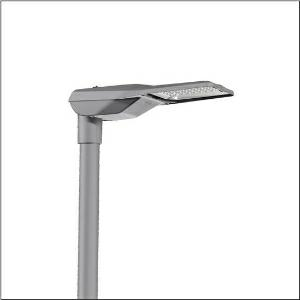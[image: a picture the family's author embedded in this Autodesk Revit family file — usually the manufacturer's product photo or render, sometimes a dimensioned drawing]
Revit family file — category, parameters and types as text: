
# Revit family: streetlight_sl_21_mini___p0_8ab_5xe2r33s08jb_3409
name_source: partatom
category: Lighting Fixtures
units: mm (PartAtom-declared; Revit-internal decimal feet)

## family parameters
Cut with Voids When Loaded = No
Host = Face
Light Source = No
Part Type = Normal
Room Calculation Point = No
Round Connector Dimension = Use Diameter
Shared = No

## types (1)
- --- (1 x LED, 11230 lm, 88.6 W, 3000K)
    Apparent Load = 89 VA
    CIE Flux Codes = 39 72 97 100 100
    Color Rendering = 70
    Color Temperature = 3000K
    Default Elevation = 1800 mm
    Description = Streetlight SL 21 mini, mast luminaire, primary light control with lens, of PMMA, primary optical cover: cover, of toughened safety glass, transparent, light distribution: P0.8aB, light emission: direct distribution, primary light characteristic: asymmetric, installation type: post-top, side-entry, LED, High Power LED, rated luminous flux: 11.230lm, luminous efficacy: 127lm/W, light colour: 730, colour temperature: 3000K, control gear: D4i, control: pre-setting: logarithmic dimming characteristic, flexible luminous flux parameterisation, time-dependent luminous flux control, constant luminous flux control, overheat protection, mains connection: 220..240V, AC, 50/60Hz, start of lifetime: 89W, end of service life: 92W, reduction: 41W, luminaire housing, of diecast aluminium, powder-coated, Siteco® metallic grey (DB 702S), corrosivity category C5 mid according to DIN EN ISO 12944, multi-level sealing system, sealing non-destructively replaceable, inclination adjustable: 0°, 5°, 10°, 15°, please order mast flange separately, length: 628mm, width: 235mm, height: 110mm, mast flange for spigot size: 42mm (side-entry): 5XC10008XM4, 60/48mm (side-entry/post-top): 5XC10108XM2, 76/60mm (side-entry/post-top): 5XC10108XM1, mounting height: 4..8m, Smart Interface above, protection rating (complete): IP66, insulation class (complete): insulation class II (safety insulation), certification: CE, ENEC, ENEC+, VDE, impact resistance: IK10, permissible operating ambient temperature for outdoor applications: -40..+50°C, standard-compliant lighting for roads and squares, packaging unit: 1 piece

Light Distribution: P0.8aB
    Height = 110 mm
    Lamp = 1 x LED
    Lamp Light Flux = 11230 lm
    Lamp Power = 88.6 W
    Lamp count = 1
    Length = 625 mm
    Luminous efficacy = 127 lm/W
    Manufacturer = Siteco
    ModVariant = No
    Model = 5XE2R33S08JB
    Number of Poles = 1
    OnlyDefault = Yes
    Power Factor = 1
    Product Name = Streetlight SL 21 mini | P0.8aB
    Product group = mast luminaire | pylon top
    ProductGroupID = 6100
    Protection Class = Protection class II
    Protection Degree = IP 66
    RLX_Detail_Level = 1
    RLX_Emergency_Light_Flux = 0 lm
    RLX_Emergency_Type = 0
    RLX_Emergency_Type_DB = No
    RlxData = <blob elided: 25877 chars, md5=df274817>
    Socket = socket
    Standby Power = 0 W
    System Light Flux = 11230 lm
    System Power = 89 W
    Type Comments = factory setting: luminous flux: 100 % | dim-lin: 254 | 915 mA
    Type Image = l_1003515.jpg
    URL = http://relux.com
    VarID = @adj_033205
    Voltage = 0 V
    Weight = 0.00 kg
    Width = 234 mm

## geometry (parser evidence)
native form markers: Blend x4, Sweep x12
no freeform markers — native parametric forms only
